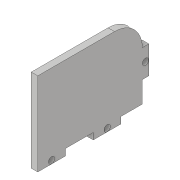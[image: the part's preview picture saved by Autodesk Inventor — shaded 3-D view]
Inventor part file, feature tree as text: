
AUTODESK INVENTOR PART (.ipt)
format: ipt  version: 2017 (Build 210142000, 142)  size: 131,072 bytes
history: native  units: in
note: dims shown in document units (in); Inventor stores cm internally (conversion verified against a paired STEP export)
features: extrude x4, sketch x4, fillet x1
ambient origin geometry x8: Origin, YZ Plane, XZ Plane, XY Plane, X Axis, Y Axis, Z Axis, Center Point
bodies: Solid1 (feature_tree)
feature tree (9):
  extrude  "Extrusion1"  Depth=2.0in
  extrude  "Extrusion2"  Depth=0.5in
  extrude  "Extrusion3"  Depth=0.5in
  fillet  "Fillet1"  Radius=0.117in
  extrude  "Extrusion4"  TaperAngle=0.0deg  [1 undecoded]
  sketch  "Sketch1"  dims[d0=1.5in d1=2.0in]
  sketch  "Sketch2"  dims[d2=0.117in d3=0.0in d4=0.5in]
  sketch  "Sketch3"  dims[d5=0.117in d6=0.5in d7=0.117in d8=0.0in]
  sketch  "Sketch4"  dims[d9=0.0in d10=0.0in d11=0.5in d12=0.117in d13=0.7874in d15=1.0in d16=0.3937in d18=1.0in d20=1.0in d21=0.0in d22=0.5in d23=0.113in d24=0.0585in d25=0.113in d26=0.113in d27=0.25in d28=0.25in d29=0.0585in d30=0.0585in d31=0.25in d32=1.0in d33=0.0in]
note: 1 required parameter value undecoded (feature->parameter linkage not recoverable at this tier; creation-order binding heuristic only, values carry confidence <= 0.55)
